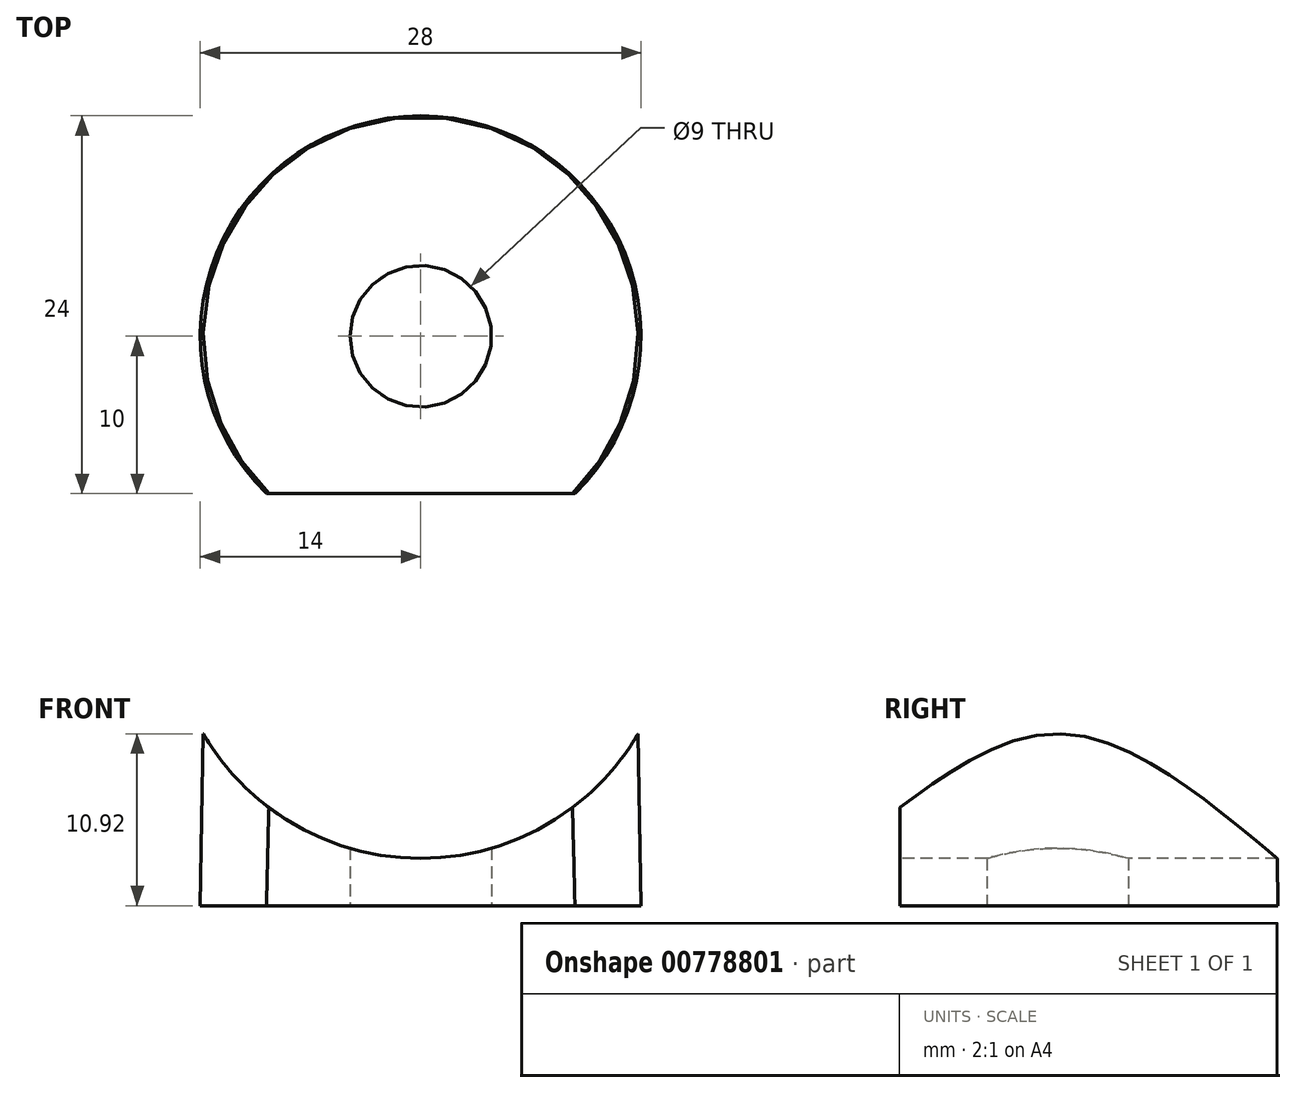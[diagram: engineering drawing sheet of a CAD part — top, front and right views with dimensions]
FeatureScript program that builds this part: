
annotation { "Feature Type Name" : "Feature", "Feature Type Description" : "" }
export const myFeature = defineFeature(function(context is Context, id is Id, definition is map)
    precondition{}
    {
        {
            var Q0;
            Q0=qCreatedBy(makeId("Top.planeOp"),FACE);
            var sketch = newSketch(context, id + "F0", { "sketchPlane" : qUnion([Q0])});
            skCircle(sketch, "E0", {"center": v(0, 0) * mm, "radius": 14 * mm});
            skSolve(sketch);
        }
        {
            var Q0;
            Q0 = qSketchRegion(id + "F0", true);
            extrude(context, id + "F1", {"entities" : qUnion([Q0]), "depth" : 12 * mm, "offsetDistance" : 25 * mm, "hasDraft" : true, "draftAngle" : 1 * degree, "draftPullDirection" : true});
        }
        {
            var Q0;
            Q0=qCreatedBy(makeId("Front.planeOp"),FACE);
            var sketch = newSketch(context, id + "F2", { "sketchPlane" : qUnion([Q0])});
            skCircle(sketch, "E1", {"center": v(0, 19) * mm, "radius": 16 * mm});
            skSolve(sketch);
        }
        {
            var Q0;
            Q0 = qSketchRegion(id + "F2", true);
            extrude(context, id + "F3", {"entities" : qUnion([Q0]), "operationType" : NewBodyOperationType.REMOVE, "oppositeDirection" : true, "depth" : 32 * mm, "offsetDistance" : 25 * mm, "symmetric" : true});
        }
        {
            var Q0;
            Q0=makeQuery(id+"F1.opExtrude","CAP_FACE",FACE,{"disambiguationData":[OSD([sQuery(id+"F0.wireOp",EDGE,"E0")])],"isStart":true});
            var sketch = newSketch(context, id + "F4", { "sketchPlane" : qUnion([Q0])});
            skCircle(sketch, "E2", {"center": v(0, 0) * mm, "radius": 4.5 * mm});
            skSolve(sketch);
        }
        {
            var Q0;
            Q0 = qSketchRegion(id + "F4", true);
            extrude(context, id + "F5", {"entities" : qUnion([Q0]), "operationType" : NewBodyOperationType.REMOVE, "oppositeDirection" : true, "depth" : 5 * mm, "offsetDistance" : 25 * mm});
        }
        {
            var Q0;
            Q0=makeQuery(id+"F1.opExtrude","CAP_FACE",FACE,{"disambiguationData":[OSD([sQuery(id+"F0.wireOp",EDGE,"E0")])],"isStart":true});
            var sketch = newSketch(context, id + "F6", { "sketchPlane" : qUnion([Q0])});
            skArc(sketch, "E3.0", {"start": v(-9.8, 10) * mm, "mid": v(0, 14) * mm, "end": v(9.8, 10) * mm});
            skLineSegment(sketch, "E4", {"start": v(-9.8, 10) * mm, "end": v(9.8, 10) * mm});
            skSolve(sketch);
        }
        {
            var Q0;
            Q0 = qSketchRegion(id + "F6", true);
            extrude(context, id + "F7", {"entities" : qUnion([Q0]), "operationType" : NewBodyOperationType.REMOVE, "endBound" : BoundingType.THROUGH_ALL, "oppositeDirection" : true, "depth" : 25 * mm, "offsetDistance" : 25 * mm});
        }
    });
